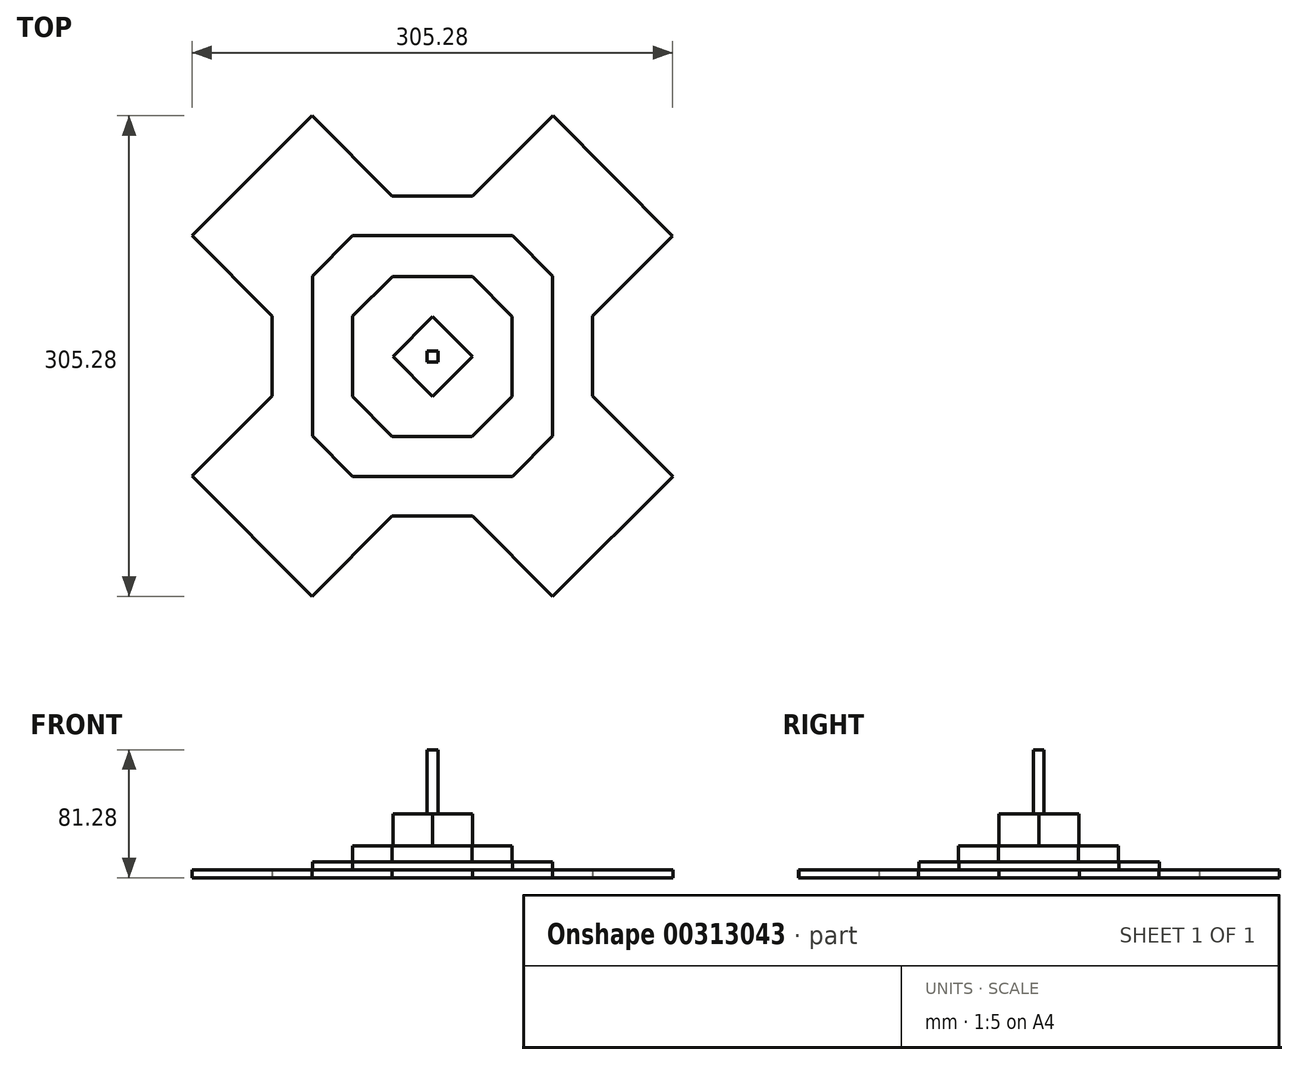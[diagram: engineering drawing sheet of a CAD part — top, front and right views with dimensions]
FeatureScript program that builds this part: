
annotation { "Feature Type Name" : "Feature", "Feature Type Description" : "" }
export const myFeature = defineFeature(function(context is Context, id is Id, definition is map)
    precondition{}
    {
        {
            var Q0;
            Q0=qCreatedBy(makeId("Top.planeOp"),FACE);
            var sketch = newSketch(context, id + "F0", { "sketchPlane" : qUnion([Q0])});
            skLineSegment(sketch, "E0.bottom", {"start": v(3.51, 3.47) * mm, "end": v(-3.51, 3.47) * mm});
            skLineSegment(sketch, "E0.top", {"start": v(3.51, -3.47) * mm, "end": v(-3.51, -3.47) * mm});
            skLineSegment(sketch, "E0.left", {"start": v(3.51, 3.47) * mm, "end": v(3.51, -3.47) * mm});
            skLineSegment(sketch, "E0.right", {"start": v(-3.51, 3.47) * mm, "end": v(-3.51, -3.47) * mm});
            skPoint(sketch, "E0.middle", {"position": v(0, 0) * mm});
            skSolve(sketch);
        }
        {
            var Q0;
            Q0=makeQuery(id+"F0.imprint","IMPRINT",FACE,{"disambiguationData":[TD([[makeQuery(id+"F0.imprint","IMPRINT",EDGE,{"derivedFrom":sQuery(id+"F0.wireOp",EDGE,"E0.bottom")}),1.0]])]});
            extrude(context, id + "F1", {"entities" : qUnion([Q0]), "depth" : 81.28 * mm});
        }
        {
            var Q0;
            Q0=qCreatedBy(makeId("Top.planeOp"),FACE);
            var sketch = newSketch(context, id + "F2", { "sketchPlane" : qUnion([Q0])});
            skLineSegment(sketch, "E1", {"start": v(-25.02, 0) * mm, "end": v(0, 25.4) * mm});
            skLineSegment(sketch, "E2", {"start": v(25.4, 0) * mm, "end": v(0, 25.4) * mm});
            skLineSegment(sketch, "E3", {"start": v(-25.02, 0) * mm, "end": v(0, -25.4) * mm});
            skLineSegment(sketch, "E4", {"start": v(25.4, 0) * mm, "end": v(0, -25.4) * mm});
            skSolve(sketch);
        }
        {
            var Q0;
            Q0=makeQuery(id+"F2.imprint","IMPRINT",FACE,{"disambiguationData":[TD([[makeQuery(id+"F2.imprint","IMPRINT",EDGE,{"derivedFrom":sQuery(id+"F2.wireOp",EDGE,"E1")}),-1.0]])]});
            extrude(context, id + "F3", {"entities" : qUnion([Q0]), "operationType" : NewBodyOperationType.ADD, "depth" : 40.64 * mm});
        }
        {
            var Q0;
            Q0=qCreatedBy(makeId("Top.planeOp"),FACE);
            var sketch = newSketch(context, id + "F4", { "sketchPlane" : qUnion([Q0])});
            skLineSegment(sketch, "E5", {"start": v(0, 0) * mm, "end": v(0, 50.78) * mm});
            skLineSegment(sketch, "E6", {"start": v(0, 50.78) * mm, "end": v(-25.43, 50.78) * mm});
            skLineSegment(sketch, "E7", {"start": v(-50.83, 0) * mm, "end": v(-50.83, 25.55) * mm});
            skLineSegment(sketch, "E8", {"start": v(-50.83, 25.55) * mm, "end": v(-25.43, 50.78) * mm});
            skLineSegment(sketch, "E9", {"start": v(-50.83, 0) * mm, "end": v(-50.83, -25.59) * mm});
            skLineSegment(sketch, "E10", {"start": v(-50.83, -25.59) * mm, "end": v(-25.6, -50.99) * mm});
            skLineSegment(sketch, "E11", {"start": v(0, 50.78) * mm, "end": v(25.44, 50.78) * mm});
            skLineSegment(sketch, "E12", {"start": v(50.67, 25.38) * mm, "end": v(25.44, 50.78) * mm});
            skLineSegment(sketch, "E13", {"start": v(50.67, 25.38) * mm, "end": v(50.67, -25.59) * mm});
            skLineSegment(sketch, "E14", {"start": v(25.27, -50.82) * mm, "end": v(50.67, -25.59) * mm});
            skLineSegment(sketch, "E15", {"start": v(-25.6, -50.99) * mm, "end": v(25.27, -50.82) * mm});
            skSolve(sketch);
        }
        {
            var Q0;
            Q0=makeQuery(id+"F4.imprint","IMPRINT",FACE,{"disambiguationData":[TD([[makeQuery(id+"F4.imprint","IMPRINT",EDGE,{"derivedFrom":sQuery(id+"F4.wireOp",EDGE,"E6")}),1.0]])]});
            extrude(context, id + "F5", {"entities" : qUnion([Q0]), "operationType" : NewBodyOperationType.ADD, "depth" : 20.32 * mm});
        }
        {
            var Q0;
            Q0=qCreatedBy(makeId("Top.planeOp"),FACE);
            var sketch = newSketch(context, id + "F6", { "sketchPlane" : qUnion([Q0])});
            skLineSegment(sketch, "E16", {"start": v(76.23, 51.06) * mm, "end": v(76.23, -50.65) * mm});
            skLineSegment(sketch, "E17", {"start": v(-76.13, -50.65) * mm, "end": v(-76.13, 51.06) * mm});
            skLineSegment(sketch, "E18", {"start": v(0, 76.67) * mm, "end": v(-50.77, 76.67) * mm});
            skLineSegment(sketch, "E19", {"start": v(-50.77, 76.67) * mm, "end": v(-76.13, 51.06) * mm});
            skLineSegment(sketch, "E20", {"start": v(0, 76.67) * mm, "end": v(50.9, 76.67) * mm});
            skLineSegment(sketch, "E21", {"start": v(50.9, 76.67) * mm, "end": v(76.23, 51.06) * mm});
            skLineSegment(sketch, "E22", {"start": v(0, -76.2) * mm, "end": v(-50.77, -76.2) * mm});
            skLineSegment(sketch, "E23", {"start": v(-50.77, -76.2) * mm, "end": v(-76.13, -50.65) * mm});
            skLineSegment(sketch, "E24", {"start": v(0, -76.2) * mm, "end": v(50.9, -76.2) * mm});
            skLineSegment(sketch, "E25", {"start": v(50.9, -76.2) * mm, "end": v(76.23, -50.65) * mm});
            skSolve(sketch);
        }
        {
            var Q0;
            Q0=makeQuery(id+"F6.imprint","IMPRINT",FACE,{"disambiguationData":[TD([[makeQuery(id+"F6.imprint","IMPRINT",EDGE,{"derivedFrom":sQuery(id+"F6.wireOp",EDGE,"E16")}),-1.0]])]});
            extrude(context, id + "F7", {"entities" : qUnion([Q0]), "operationType" : NewBodyOperationType.ADD, "depth" : 10.16 * mm});
        }
        {
            var Q0;
            Q0=qCreatedBy(makeId("Top.planeOp"),FACE);
            var sketch = newSketch(context, id + "F8", { "sketchPlane" : qUnion([Q0])});
            skPoint(sketch, "E26.endSnap0", {"position": v(0, 50.79) * mm});
            skLineSegment(sketch, "E27", {"start": v(0, -101.52) * mm, "end": v(25.53, -101.52) * mm});
            skLineSegment(sketch, "E28", {"start": v(25.53, -101.52) * mm, "end": v(-25.51, -101.52) * mm});
            skLineSegment(sketch, "E29", {"start": v(-76.49, -152.42) * mm, "end": v(-25.51, -101.52) * mm});
            skLineSegment(sketch, "E30", {"start": v(-152.58, -76.07) * mm, "end": v(-76.49, -152.42) * mm});
            skLineSegment(sketch, "E31", {"start": v(-101.72, -25.3) * mm, "end": v(-152.58, -76.07) * mm});
            skLineSegment(sketch, "E32", {"start": v(-101.72, -25.3) * mm, "end": v(-101.72, 25.74) * mm});
            skLineSegment(sketch, "E33", {"start": v(-152.63, 76.72) * mm, "end": v(-101.72, 25.74) * mm});
            skLineSegment(sketch, "E34", {"start": v(-76.28, 152.81) * mm, "end": v(-152.63, 76.72) * mm});
            skLineSegment(sketch, "E35", {"start": v(-25.5, 101.95) * mm, "end": v(-76.28, 152.81) * mm});
            skLineSegment(sketch, "E36", {"start": v(101.75, 25.73) * mm, "end": v(101.75, -25.3) * mm});
            skLineSegment(sketch, "E37", {"start": v(152.65, -76.28) * mm, "end": v(101.75, -25.3) * mm});
            skLineSegment(sketch, "E38", {"start": v(76.3, -152.38) * mm, "end": v(152.65, -76.28) * mm});
            skLineSegment(sketch, "E39", {"start": v(25.53, -101.52) * mm, "end": v(76.3, -152.38) * mm});
            skLineSegment(sketch, "E40", {"start": v(-25.5, 101.95) * mm, "end": v(25.54, 101.95) * mm});
            skLineSegment(sketch, "E41", {"start": v(76.51, 152.86) * mm, "end": v(25.54, 101.95) * mm});
            skLineSegment(sketch, "E42", {"start": v(152.6, 76.5) * mm, "end": v(76.51, 152.86) * mm});
            skLineSegment(sketch, "E43", {"start": v(101.75, 25.73) * mm, "end": v(152.6, 76.5) * mm});
            skSolve(sketch);
        }
        {
            var Q0;
            {var subQ2=sQuery(id+"F8.wireOp",EDGE,"E29");Q0=makeQuery(id+"F8.imprint","IMPRINT",FACE,{"disambiguationData":[TD([[makeQuery(id+"F8.imprint","IMPRINT",EDGE,{"derivedFrom":subQ2}),1.0]])]});}
            extrude(context, id + "F9", {"entities" : qUnion([Q0]), "operationType" : NewBodyOperationType.ADD, "depth" : 5.08 * mm});
        }
    });
